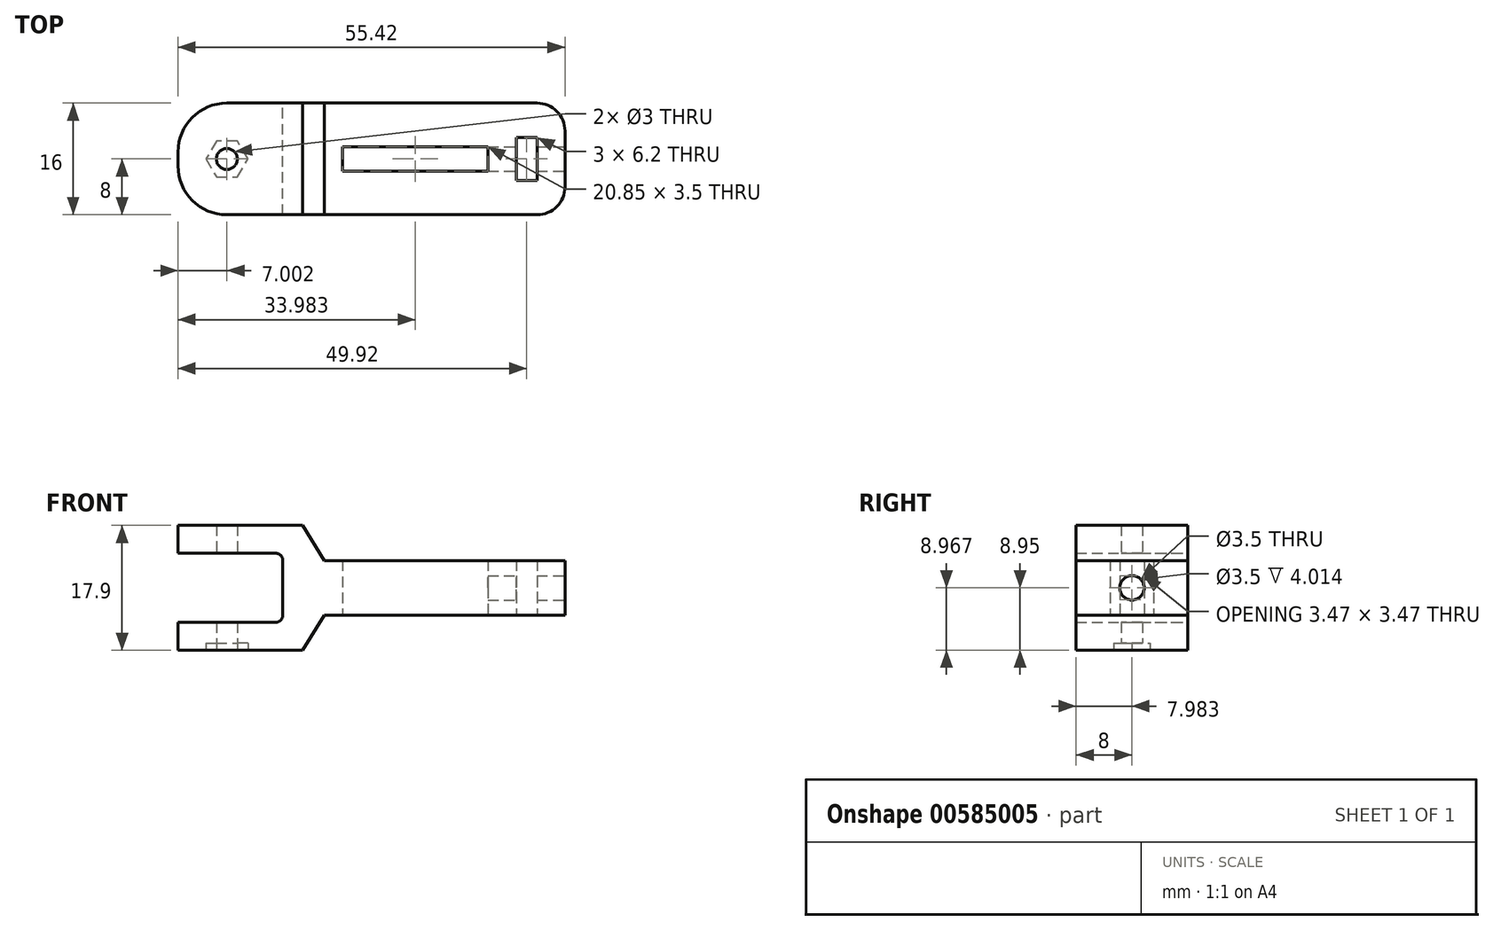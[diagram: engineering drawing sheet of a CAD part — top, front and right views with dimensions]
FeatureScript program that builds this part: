
annotation { "Feature Type Name" : "Feature", "Feature Type Description" : "" }
export const myFeature = defineFeature(function(context is Context, id is Id, definition is map)
    precondition{}
    {
        {
            var Q0;
            Q0=qCreatedBy(makeId("Top.planeOp"),FACE);
            var sketch = newSketch(context, id + "F0", { "sketchPlane" : qUnion([Q0])});
            skLineSegment(sketch, "E0.bottom", {"start": v(-17.5, -8) * mm, "end": v(13.5, -8) * mm});
            skLineSegment(sketch, "E0.top", {"start": v(-17.5, 8) * mm, "end": v(13.5, 8) * mm});
            skLineSegment(sketch, "E0.left", {"start": v(-17.5, -8) * mm, "end": v(-17.5, 8) * mm});
            skLineSegment(sketch, "E0.right", {"start": v(17.5, -4) * mm, "end": v(17.5, 4) * mm});
            skPoint(sketch, "E0.middle", {"position": v(0, 0) * mm});
            skLineSegment(sketch, "E1.bottom", {"start": v(10.5, -3.1) * mm, "end": v(13.5, -3.1) * mm});
            skLineSegment(sketch, "E1.top", {"start": v(10.5, 3.1) * mm, "end": v(13.5, 3.1) * mm});
            skLineSegment(sketch, "E1.left", {"start": v(10.5, -3.1) * mm, "end": v(10.5, 3.1) * mm});
            skLineSegment(sketch, "E1.right", {"start": v(13.5, -3.1) * mm, "end": v(13.5, 3.1) * mm});
            skPoint(sketch, "E1.middle", {"position": v(12, 0) * mm});
            skLineSegment(sketch, "E2.bottom", {"start": v(-14.36, -1.75) * mm, "end": v(6.49, -1.75) * mm});
            skLineSegment(sketch, "E2.top", {"start": v(-14.36, 1.75) * mm, "end": v(6.49, 1.75) * mm});
            skLineSegment(sketch, "E2.left", {"start": v(-14.36, -1.75) * mm, "end": v(-14.36, 1.75) * mm});
            skLineSegment(sketch, "E2.right", {"start": v(6.49, -1.75) * mm, "end": v(6.49, 1.75) * mm});
            skPoint(sketch, "E2.middle", {"position": v(-3.94, 0) * mm});
            skPoint(sketch, "E3.visualSharp", {"position": v(17.5, 8) * mm});
            skArc(sketch, "E3.filletArc", {"start": v(17.5, 4) * mm, "mid": v(16.33, 6.83) * mm, "end": v(13.5, 8) * mm});
            skPoint(sketch, "E4.visualSharp", {"position": v(17.5, -8) * mm});
            skArc(sketch, "E4.filletArc", {"start": v(13.5, -8) * mm, "mid": v(16.33, -6.83) * mm, "end": v(17.5, -4) * mm});
            skSolve(sketch);
        }
        {
            var Q0;
            Q0=makeQuery(id+"F0.imprint","IMPRINT",FACE,{"disambiguationData":[TD([[makeQuery(id+"F0.imprint","IMPRINT",EDGE,{"derivedFrom":sQuery(id+"F0.wireOp",EDGE,"E0.bottom")}),1.0]])]});
            extrude(context, id + "F1", {"entities" : qUnion([Q0]), "depth" : 3.9 * mm, "offsetDistance" : 25 * mm, "hasSecondDirection" : true, "secondDirectionOppositeDirection" : true, "secondDirectionDepth" : 3.9 * mm});
        }
        {
            var Q0;
            Q0=makeQuery(id+"F1.opExtrude","SWEPT_FACE",FACE,{"disambiguationData":[OSD([sQuery(id+"F0.wireOp",EDGE,"E0.right")])]});
            var sketch = newSketch(context, id + "F2", { "sketchPlane" : qUnion([Q0])});
            skCircle(sketch, "E5", {"center": v(0, 0) * mm, "radius": 1.75 * mm});
            skSolve(sketch);
        }
        {
            var Q0;
            Q0 = qSketchRegion(id + "F2", true);
            extrude(context, id + "F3", {"entities" : qUnion([Q0]), "operationType" : NewBodyOperationType.REMOVE, "oppositeDirection" : true, "depth" : 16.2 * mm, "offsetDistance" : 25 * mm});
        }
        {
            var Q0;
            Q0=qCreatedBy(makeId("Front.planeOp"),FACE);
            var sketch = newSketch(context, id + "F4", { "sketchPlane" : qUnion([Q0])});
            skLineSegment(sketch, "E6.left", {"start": v(-22.92, -3.95) * mm, "end": v(-22.92, 3.95) * mm});
            skLineSegment(sketch, "E7.bottom", {"start": v(-20.07, -8.95) * mm, "end": v(-37.92, -8.95) * mm});
            skLineSegment(sketch, "E7.top", {"start": v(-23.92, -4.95) * mm, "end": v(-37.92, -4.95) * mm});
            skLineSegment(sketch, "E7.right", {"start": v(-37.92, -8.95) * mm, "end": v(-37.92, -4.95) * mm});
            skLineSegment(sketch, "E8.MirrorCS", {"start": v(-23.92, 4.95) * mm, "end": v(-37.92, 4.95) * mm});
            skLineSegment(sketch, "E9.MirrorCS", {"start": v(-37.92, 8.95) * mm, "end": v(-37.92, 4.95) * mm});
            skArc(sketch, "E10.filletArc", {"start": v(-23.92, -4.95) * mm, "mid": v(-23.21, -4.66) * mm, "end": v(-22.92, -3.95) * mm});
            skArc(sketch, "E11.filletArc", {"start": v(-22.92, 3.95) * mm, "mid": v(-23.21, 4.66) * mm, "end": v(-23.92, 4.95) * mm});
            skPoint(sketch, "E12", {"position": v(-19.91, 0) * mm});
            skLineSegment(sketch, "E13", {"start": v(-20.07, -8.95) * mm, "end": v(-16.95, -3.84) * mm});
            skLineSegment(sketch, "E14.MirrorCS", {"start": v(-20.07, 8.95) * mm, "end": v(-16.95, 3.84) * mm});
            skLineSegment(sketch, "E15.MirrorCS", {"start": v(-20.07, 8.95) * mm, "end": v(-37.92, 8.95) * mm});
            skLineSegment(sketch, "E16", {"start": v(-16.95, -3.84) * mm, "end": v(-16.95, 3.84) * mm});
            skSolve(sketch);
        }
        {
            var Q0;
            Q0 = qSketchRegion(id + "F4", true);
            extrude(context, id + "F5", {"entities" : qUnion([Q0]), "operationType" : NewBodyOperationType.ADD, "depth" : 8 * mm, "offsetDistance" : 25 * mm, "hasSecondDirection" : true, "secondDirectionOppositeDirection" : true, "secondDirectionDepth" : 8 * mm});
        }
        {
            var Q0;
            Q0=makeQuery(id+"F5.opExtrude","CAP_EDGE",EDGE,{"disambiguationData":[OSD([sQuery(id+"F4.wireOp",EDGE,"E7.right")])],"isStart":false});
            var Q1;
            Q1=makeQuery(id+"F5.opExtrude","CAP_EDGE",EDGE,{"disambiguationData":[OSD([sQuery(id+"F4.wireOp",EDGE,"E9.MirrorCS")])],"isStart":false});
            var Q2;
            Q2=makeQuery(id+"F5.opExtrude","CAP_EDGE",EDGE,{"disambiguationData":[OSD([sQuery(id+"F4.wireOp",EDGE,"E9.MirrorCS")])],"isStart":true});
            var Q3;
            Q3=makeQuery(id+"F5.opExtrude","CAP_EDGE",EDGE,{"disambiguationData":[OSD([sQuery(id+"F4.wireOp",EDGE,"E7.right")])],"isStart":true});
            fillet(context, id + "F6", {"entities" : qUnion([Q0, Q1, Q2, Q3]), "radius" : 7 * mm, "tangentPropagation" : true, "allowEdgeOverflow" : false});
        }
        {
            var Q0;
            Q0=makeQuery(id+"F5.opExtrude","SWEPT_FACE",FACE,{"disambiguationData":[OSD([sQuery(id+"F4.wireOp",EDGE,"E7.bottom")])]});
            var sketch = newSketch(context, id + "F7", { "sketchPlane" : qUnion([Q0])});
            skCircle(sketch, "E17", {"center": v(-30.92, 0) * mm, "radius": 1.5 * mm});
            skSolve(sketch);
        }
        {
            var Q0;
            Q0=makeQuery(id+"F7.imprint","IMPRINT",FACE,{"disambiguationData":[TD([[makeQuery(id+"F7.imprint","IMPRINT",EDGE,{"derivedFrom":sQuery(id+"F7.wireOp",EDGE,"E17")}),1.0]])]});
            extrude(context, id + "F8", {"entities" : qUnion([Q0]), "operationType" : NewBodyOperationType.REMOVE, "oppositeDirection" : true, "depth" : 25 * mm, "offsetDistance" : 25 * mm});
        }
        {
            var Q0;
            Q0=makeQuery(id+"F5.opExtrude","SWEPT_FACE",FACE,{"disambiguationData":[OSD([sQuery(id+"F4.wireOp",EDGE,"E7.bottom")])]});
            var sketch = newSketch(context, id + "F9", { "sketchPlane" : qUnion([Q0])});
            skCircle(sketch, "E18.cCircle", {"center": v(-30.92, 0) * mm, "radius": 3 * mm, "construction": true});
            skLineSegment(sketch, "E18.0", {"start": v(-27.92, 0) * mm, "end": v(-29.42, -2.6) * mm});
            skLineSegment(sketch, "E18.1", {"start": v(-29.42, -2.6) * mm, "end": v(-32.42, -2.6) * mm});
            skLineSegment(sketch, "E18.2", {"start": v(-32.42, -2.6) * mm, "end": v(-33.92, 0) * mm});
            skLineSegment(sketch, "E18.3", {"start": v(-33.92, 0) * mm, "end": v(-32.42, 2.6) * mm});
            skLineSegment(sketch, "E18.4", {"start": v(-32.42, 2.6) * mm, "end": v(-29.42, 2.6) * mm});
            skLineSegment(sketch, "E18.5", {"start": v(-29.42, 2.6) * mm, "end": v(-27.92, 0) * mm});
            skSolve(sketch);
        }
        {
            var Q0;
            Q0=makeQuery(id+"F9.imprint","IMPRINT",FACE,{"disambiguationData":[TD([[makeQuery(id+"F9.imprint","IMPRINT",EDGE,{"derivedFrom":sQuery(id+"F9.wireOp",EDGE,"E18.0")}),-1.0]])]});
            extrude(context, id + "F10", {"entities" : qUnion([Q0]), "operationType" : NewBodyOperationType.REMOVE, "oppositeDirection" : true, "depth" : 1 * mm, "offsetDistance" : 25 * mm});
        }
    });
